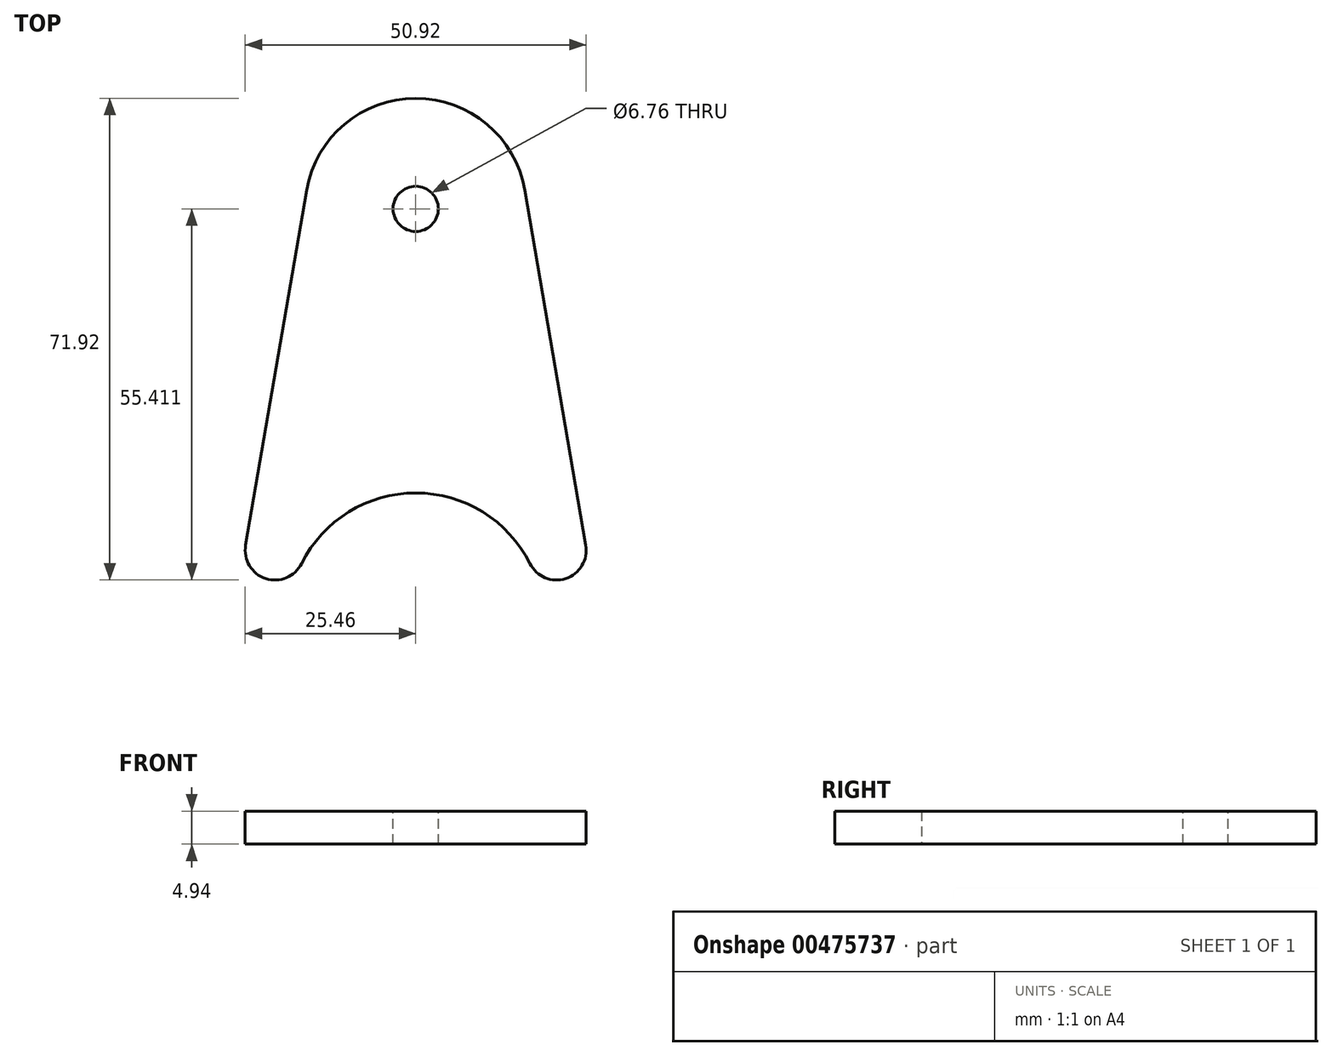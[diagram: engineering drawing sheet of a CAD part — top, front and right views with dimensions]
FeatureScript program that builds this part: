
annotation { "Feature Type Name" : "Feature", "Feature Type Description" : "" }
export const myFeature = defineFeature(function(context is Context, id is Id, definition is map)
    precondition{}
    {
        {
            var Q0;
            Q0=qCreatedBy(makeId("Top.planeOp"),FACE);
            var sketch = newSketch(context, id + "F0", { "sketchPlane" : qUnion([Q0])});
            skLineSegment(sketch, "E0", {"start": v(0, -49.37) * mm, "end": v(0, 65.55) * mm, "construction": true});
            skArc(sketch, "E1", {"start": v(0, 37.67) * mm, "mid": v(-10.64, 33.79) * mm, "end": v(-16.27, 23.96) * mm});
            skArc(sketch, "E2", {"start": v(0, -21.26) * mm, "mid": v(-10.02, -24.1) * mm, "end": v(-17.04, -31.8) * mm});
            skLineSegment(sketch, "E3", {"start": v(-25.4, -29.06) * mm, "end": v(-16.27, 23.96) * mm});
            skArc(sketch, "E4.MirrorCS", {"start": v(0, 37.67) * mm, "mid": v(10.64, 33.79) * mm, "end": v(16.27, 23.96) * mm});
            skLineSegment(sketch, "E5.MirrorCS", {"start": v(25.4, -29.06) * mm, "end": v(16.27, 23.96) * mm});
            skArc(sketch, "E6.MirrorCS", {"start": v(0, -21.26) * mm, "mid": v(10.02, -24.1) * mm, "end": v(17.04, -31.8) * mm});
            skArc(sketch, "E7", {"start": v(-25.4, -29.06) * mm, "mid": v(-22.4, -34.03) * mm, "end": v(-17.04, -31.8) * mm});
            skArc(sketch, "E8.MirrorCS", {"start": v(25.4, -29.06) * mm, "mid": v(22.4, -34.03) * mm, "end": v(17.04, -31.8) * mm});
            skSolve(sketch);
        }
        {
            var Q0;
            Q0 = qSketchRegion(id + "F0", true);
            extrude(context, id + "F1", {"entities" : qUnion([Q0]), "depth" : 4.94 * mm});
        }
        {
            var Q0;
            Q0=makeQuery(id+"F1.opExtrude","CAP_FACE",FACE,{"disambiguationData":[OSD([sQuery(id+"F0.wireOp",EDGE,"E1"),sQuery(id+"F0.wireOp",EDGE,"E2"),sQuery(id+"F0.wireOp",EDGE,"E3"),sQuery(id+"F0.wireOp",EDGE,"E4.MirrorCS"),sQuery(id+"F0.wireOp",EDGE,"E5.MirrorCS"),sQuery(id+"F0.wireOp",EDGE,"E6.MirrorCS"),sQuery(id+"F0.wireOp",EDGE,"E7"),sQuery(id+"F0.wireOp",EDGE,"E8.MirrorCS")])],"isStart":false});
            var sketch = newSketch(context, id + "F2", { "sketchPlane" : qUnion([Q0])});
            skPoint(sketch, "E9", {"position": v(0, 21.16) * mm});
            skSolve(sketch);
        }
        {
            var Q0;
            Q0=sQuery(id+"F2.wireOp",VERTEX,"E9");
            var Q1;
            Q1=makeQuery(id+"F1.opExtrude","SWEPT_BODY",BODY,{"disambiguationData":[OSD([sQuery(id+"F0.wireOp",EDGE,"E1"),sQuery(id+"F0.wireOp",EDGE,"E2"),sQuery(id+"F0.wireOp",EDGE,"E3"),sQuery(id+"F0.wireOp",EDGE,"E4.MirrorCS"),sQuery(id+"F0.wireOp",EDGE,"E5.MirrorCS"),sQuery(id+"F0.wireOp",EDGE,"E6.MirrorCS"),sQuery(id+"F0.wireOp",EDGE,"E7"),sQuery(id+"F0.wireOp",EDGE,"E8.MirrorCS")])]});
            hole(context, id + "F3", {"style" : HoleStyle.SIMPLE, "endStyle" : HoleEndStyle.THROUGH, "standardTappedOrClearance" : lookupTablePath({ "standard" : "ANSI", "fit" : "Normal (ASME)", "size" : "1/4", "type" : "Clearance" }), "standardBlindInLast" : lookupTablePath({ "fit" : "Free", "standard" : "ANSI", "size" : "1/4", "type" : "Clearance" }), "holeDiameter" : 6.76 * mm, "isTappedThrough" : true, "tappedDepth" : 12.7 * mm, "tapClearance" : 3, "locations" : qUnion([Q0]), "scope" : qUnion([Q1])});
        }
    });
